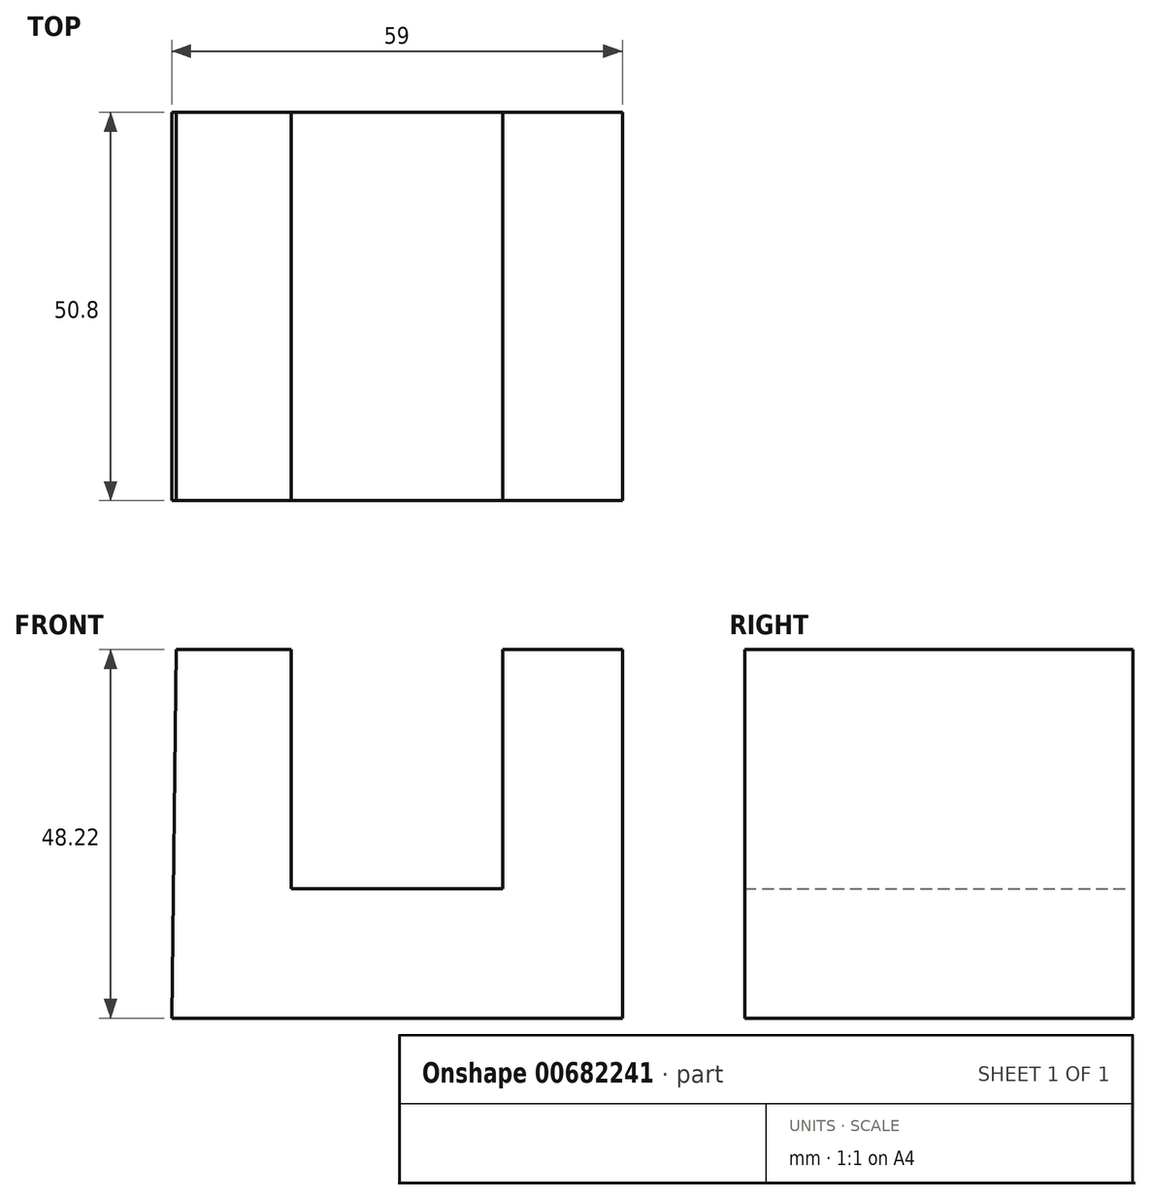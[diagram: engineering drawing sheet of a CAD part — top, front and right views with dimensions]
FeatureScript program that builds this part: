
annotation { "Feature Type Name" : "Feature", "Feature Type Description" : "" }
export const myFeature = defineFeature(function(context is Context, id is Id, definition is map)
    precondition{}
    {
        {
            var Q0;
            Q0=qCreatedBy(makeId("Front.planeOp"),FACE);
            var sketch = newSketch(context, id + "F0", { "sketchPlane" : qUnion([Q0])});
            skLineSegment(sketch, "E0", {"start": v(-73.04, 48.22) * mm, "end": v(-57.95, 48.22) * mm});
            skLineSegment(sketch, "E1", {"start": v(-57.95, 48.22) * mm, "end": v(-57.95, 16.9) * mm});
            skLineSegment(sketch, "E2", {"start": v(-57.95, 16.9) * mm, "end": v(-30.27, 16.9) * mm});
            skLineSegment(sketch, "E3", {"start": v(-30.27, 16.9) * mm, "end": v(-30.27, 48.22) * mm});
            skLineSegment(sketch, "E4", {"start": v(-30.27, 48.22) * mm, "end": v(-14.6, 48.22) * mm});
            skLineSegment(sketch, "E5", {"start": v(-14.6, 48.22) * mm, "end": v(-14.6, 0) * mm});
            skLineSegment(sketch, "E6", {"start": v(-14.6, 0) * mm, "end": v(-73.61, 0) * mm});
            skLineSegment(sketch, "E7", {"start": v(-73.61, 0) * mm, "end": v(-73.04, 48.22) * mm});
            skSolve(sketch);
        }
        {
            var Q0;
            Q0 = qSketchRegion(id + "F0", true);
            extrude(context, id + "F1", {"entities" : qUnion([Q0]), "depth" : 50.8 * mm, "offsetDistance" : 25.4 * mm});
        }
    });
